# Revit family: Faucet-Lavatory-KOHLER-Vive-K-23966IN_1
name_source: partatom
category: Plumbing Fixtures
units: mm (PartAtom-declared; Revit-internal decimal feet)

## family parameters
Cut with Voids When Loaded = No
Host = Face
Maintain Annotation Orientation = No
OmniClass Number = 23.31.11.00
Part Type = Normal
Room Calculation Point = No
Round Connector Dimension = Use Diameter
Shared = No

## types (4) — shared parameters
ADA Compliant = No
Assembly Code = D2010
CW Connection = Yes
Cold Water Inlet = Cold Water Inlet
Date Modified = 12/22/2022
Default Elevation = 36"
Description = Single Control Lav Faucet Without Drain
Drain Included = No
Flow Rate = 2 GPM
HW Connection = Yes
Handle Clearance = 0"
Height = 9 5/8"
Hot Water Inlet = Hot Water Inlet
Length = 4 5/8"
Manufacturer = Kohler Co.
Master Format 2014 = 22 41 39
Master Format 2014 Name = Residential Faucets, Supplies, and Trim
Material = Premium Metal Construction
Pressure = 45.00 psi
Product Name = Vive
Spout Reach = 4 5/8"
URL = https://www.kohler.co.in
Vent Connection = No
Waste Connection = No
Waste Water Outlet = Waste Water Outlet
WaterSense Certified = No
Width = 1 15/16"

## per-type parameters (varying)
| type | Finish | Model | Product Page URL | Type |
| CP-Polished Chrome | Kohler-Metal-CP-Polished_Chrome | K-23966IN-4ND-CP | https://www.kohler.co.in | 1 |
| AF-Vibrant French Gold | Kohler-Metal-AF-Vibrant_French_Gold | K-23966IN-4ND-AF | https://www.kohler.co.in | 2 |
| RGD-Polished Rose Gold | Kohler-Metal-RGD-Polished_Rose_Gold | K-23966IN-4ND-RGD | https://www.kohler.co.in | 3 |
| BL-Matte Black | Kohler-Metal-BL-Matte_Black | K-23966IN-4ND-BL |  | 4 |

## geometry (parser evidence)
native form markers: Sweep x4
no freeform markers — native parametric forms only
